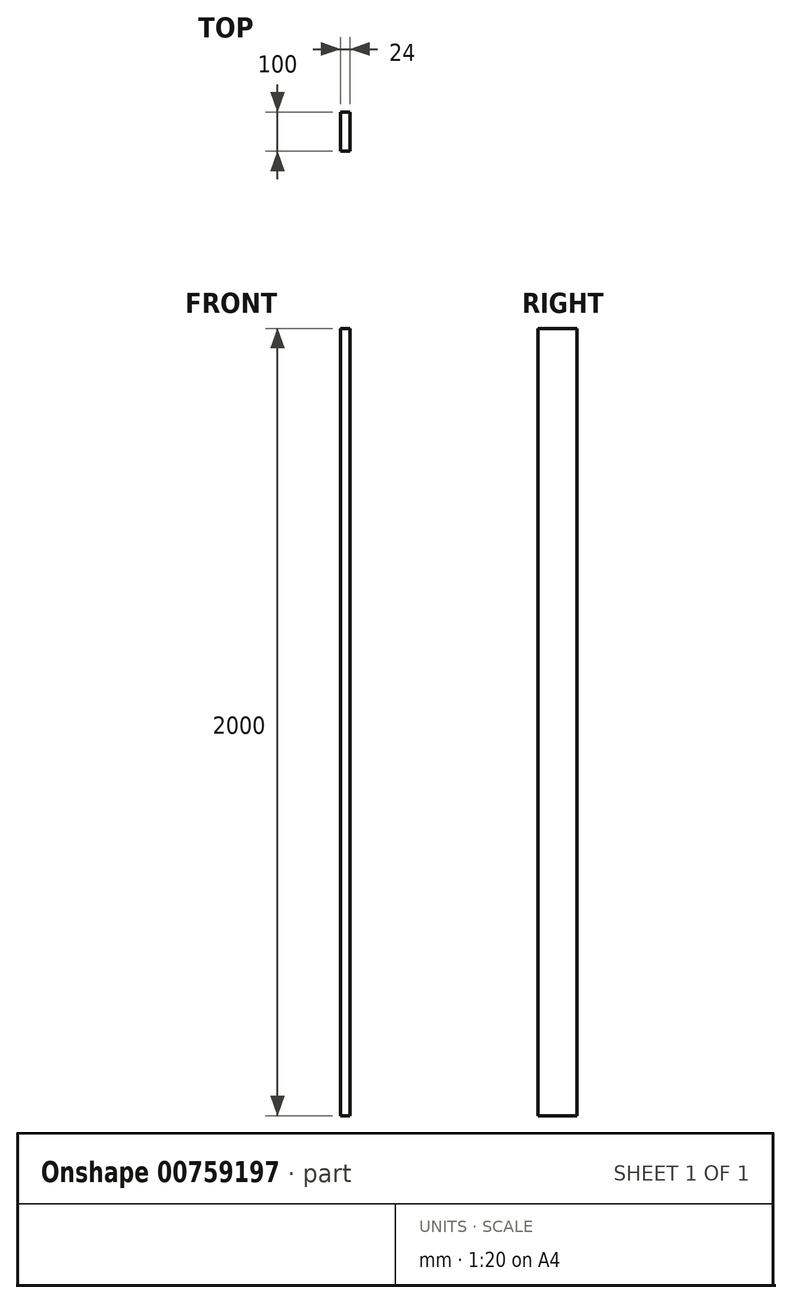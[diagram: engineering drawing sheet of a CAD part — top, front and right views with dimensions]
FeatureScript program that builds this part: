
annotation { "Feature Type Name" : "Feature", "Feature Type Description" : "" }
export const myFeature = defineFeature(function(context is Context, id is Id, definition is map)
    precondition{}
    {
        {
            var Q0;
            Q0=qCreatedBy(makeId("Top.planeOp"),FACE);
            var sketch = newSketch(context, id + "F0", { "sketchPlane" : qUnion([Q0])});
            skLineSegment(sketch, "E0.bottom", {"start": v(24, 0) * mm, "end": v(0, 0) * mm});
            skLineSegment(sketch, "E0.top", {"start": v(24, 100) * mm, "end": v(0, 100) * mm});
            skLineSegment(sketch, "E0.left", {"start": v(24, 0) * mm, "end": v(24, 100) * mm});
            skLineSegment(sketch, "E0.right", {"start": v(0, 0) * mm, "end": v(0, 100) * mm});
            skSolve(sketch);
        }
        {
            var Q0;
            Q0 = qSketchRegion(id + "F0", true);
            extrude(context, id + "F1", {"entities" : qUnion([Q0]), "depth" : 2000 * mm, "offsetDistance" : 25 * mm});
        }
    });
